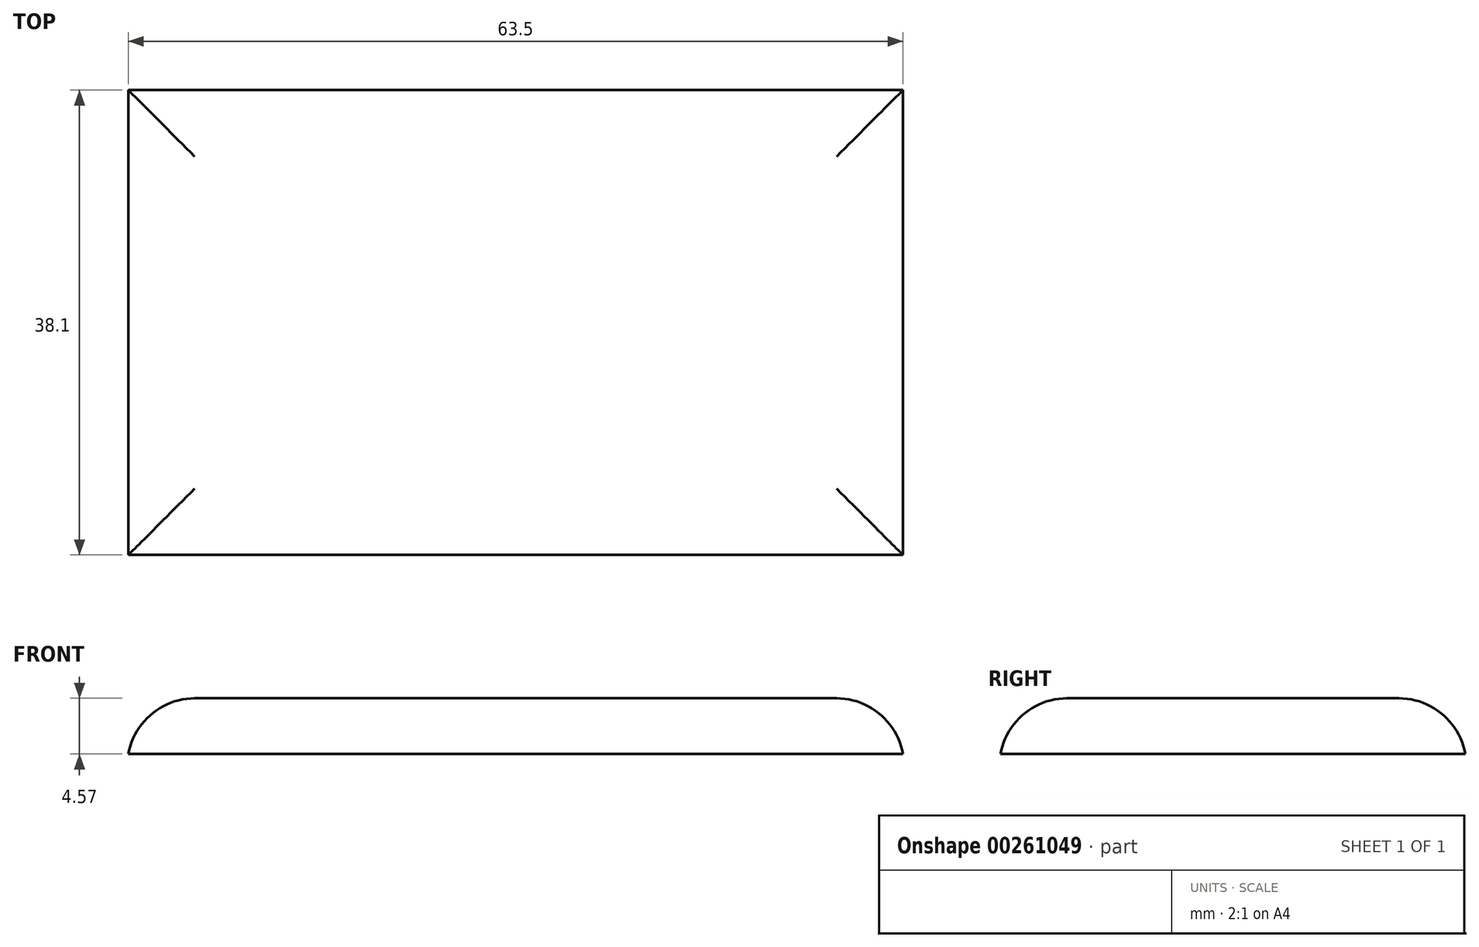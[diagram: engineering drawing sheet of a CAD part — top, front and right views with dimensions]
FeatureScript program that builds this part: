
annotation { "Feature Type Name" : "Feature", "Feature Type Description" : "" }
export const myFeature = defineFeature(function(context is Context, id is Id, definition is map)
    precondition{}
    {
        {
            var Q0;
            Q0=qCreatedBy(makeId("Top.planeOp"),FACE);
            var sketch = newSketch(context, id + "F0", { "sketchPlane" : qUnion([Q0])});
            skLineSegment(sketch, "E0.bottom", {"start": v(-31.75, 19.05) * mm, "end": v(31.75, 19.05) * mm});
            skLineSegment(sketch, "E0.top", {"start": v(-31.75, -19.05) * mm, "end": v(31.75, -19.05) * mm});
            skLineSegment(sketch, "E0.left", {"start": v(-31.75, 19.05) * mm, "end": v(-31.75, -19.05) * mm});
            skLineSegment(sketch, "E0.right", {"start": v(31.75, 19.05) * mm, "end": v(31.75, -19.05) * mm});
            skPoint(sketch, "E0.middle", {"position": v(0, 0) * mm});
            skSolve(sketch);
        }
        {
            var Q0;
            Q0 = qSketchRegion(id + "F0", true);
            extrude(context, id + "F1", {"entities" : qUnion([Q0]), "depth" : 4.57 * mm});
        }
        {
            var Q0;
            Q0=makeQuery(id+"F1.opExtrude","CAP_EDGE",EDGE,{"disambiguationData":[OSD([sQuery(id+"F0.wireOp",EDGE,"E0.left")])],"isStart":false});
            var Q1;
            Q1=makeQuery(id+"F1.opExtrude","CAP_EDGE",EDGE,{"disambiguationData":[OSD([sQuery(id+"F0.wireOp",EDGE,"E0.right")])],"isStart":false});
            var Q2;
            Q2=makeQuery(id+"F1.opExtrude","CAP_EDGE",EDGE,{"disambiguationData":[OSD([sQuery(id+"F0.wireOp",EDGE,"E0.top")])],"isStart":false});
            var Q3;
            Q3=makeQuery(id+"F1.opExtrude","CAP_EDGE",EDGE,{"disambiguationData":[OSD([sQuery(id+"F0.wireOp",EDGE,"E0.bottom")])],"isStart":false});
            fillet(context, id + "F2", {"entities" : qUnion([Q0, Q1, Q2, Q3]), "radius" : 5.52 * mm, "tangentPropagation" : true, "allowEdgeOverflow" : false});
        }
        {
            var Q0;
            Q0=qCreatedBy(makeId("Front.planeOp"),FACE);
            var sketch = newSketch(context, id + "F3", { "sketchPlane" : qUnion([Q0])});
            skArc(sketch, "E1", {"start": v(21.9, 4.57) * mm, "mid": v(0.9, 15.4) * mm, "end": v(-20.06, 4.52) * mm});
            skSolve(sketch);
        }
        {
            var Q0;
            Q0=sQuery(id+"F3.wireOp",EDGE,"E1");
            extrude(context, id + "F4", {"bodyType" : ToolBodyType.SURFACE, "surfaceEntities" : qUnion([Q0]), "depth" : 5.08 * mm});
        }
    });
